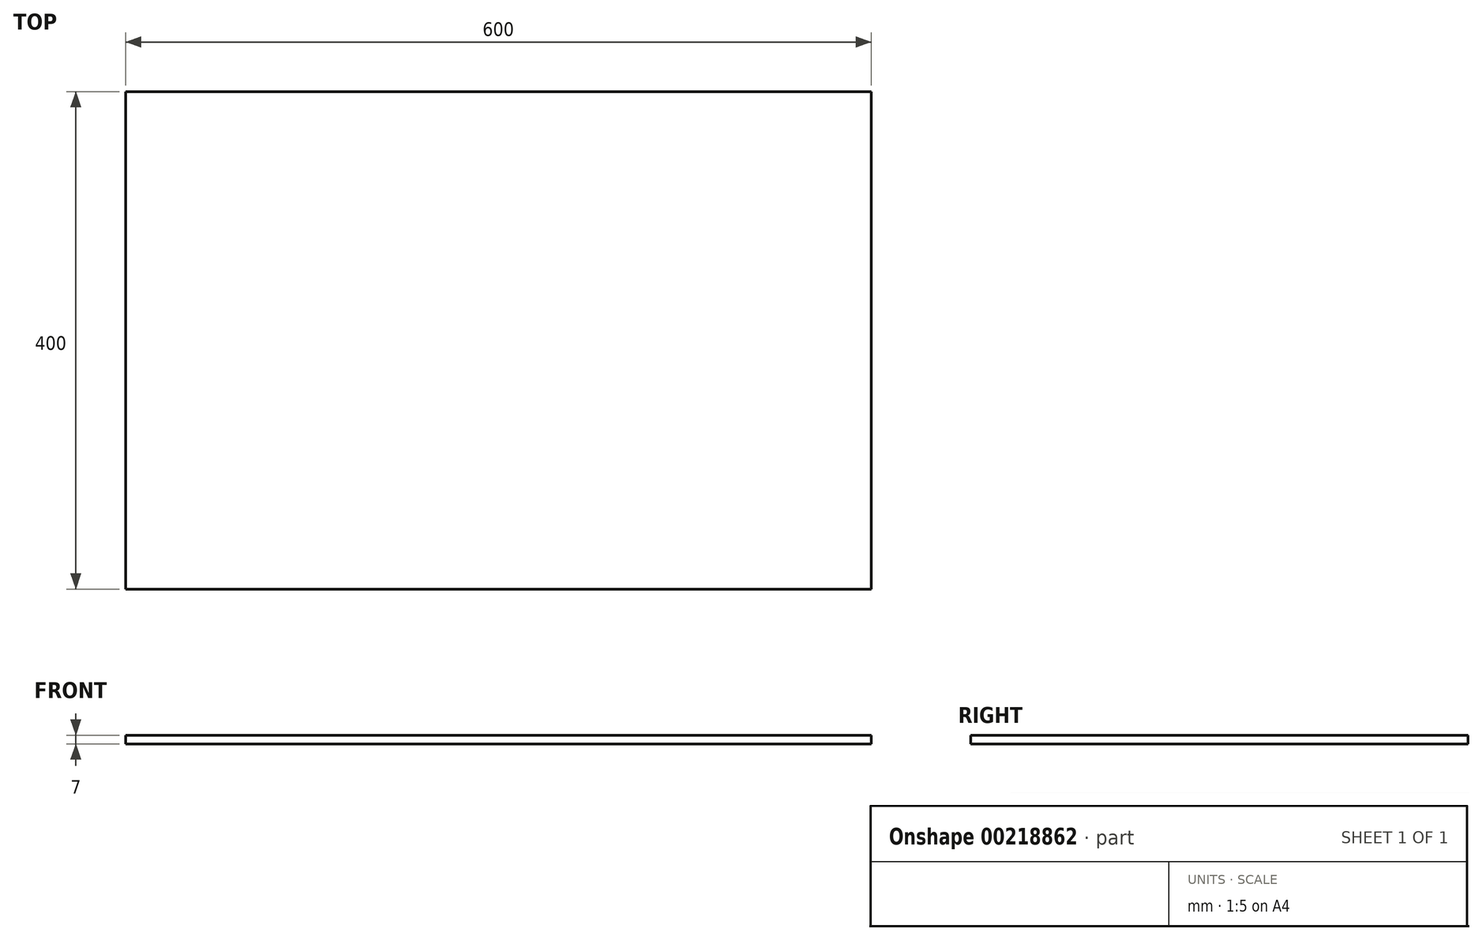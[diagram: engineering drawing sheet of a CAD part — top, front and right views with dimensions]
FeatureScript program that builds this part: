
annotation { "Feature Type Name" : "Feature", "Feature Type Description" : "" }
export const myFeature = defineFeature(function(context is Context, id is Id, definition is map)
    precondition{}
    {
        {
            var Q0;
            Q0=qCreatedBy(makeId("Top.planeOp"),FACE);
            var sketch = newSketch(context, id + "F0", { "sketchPlane" : qUnion([Q0])});
            skLineSegment(sketch, "E0.bottom", {"start": v(-304.22, 268.43) * mm, "end": v(295.78, 268.43) * mm});
            skLineSegment(sketch, "E0.top", {"start": v(-304.22, -131.57) * mm, "end": v(295.78, -131.57) * mm});
            skLineSegment(sketch, "E0.left", {"start": v(-304.22, 268.43) * mm, "end": v(-304.22, -131.57) * mm});
            skLineSegment(sketch, "E0.right", {"start": v(295.78, 268.43) * mm, "end": v(295.78, -131.57) * mm});
            skSolve(sketch);
        }
        {
            var Q0;
            Q0 = qSketchRegion(id + "F0", true);
            extrude(context, id + "F1", {"entities" : qUnion([Q0]), "depth" : 7 * mm});
        }
    });
